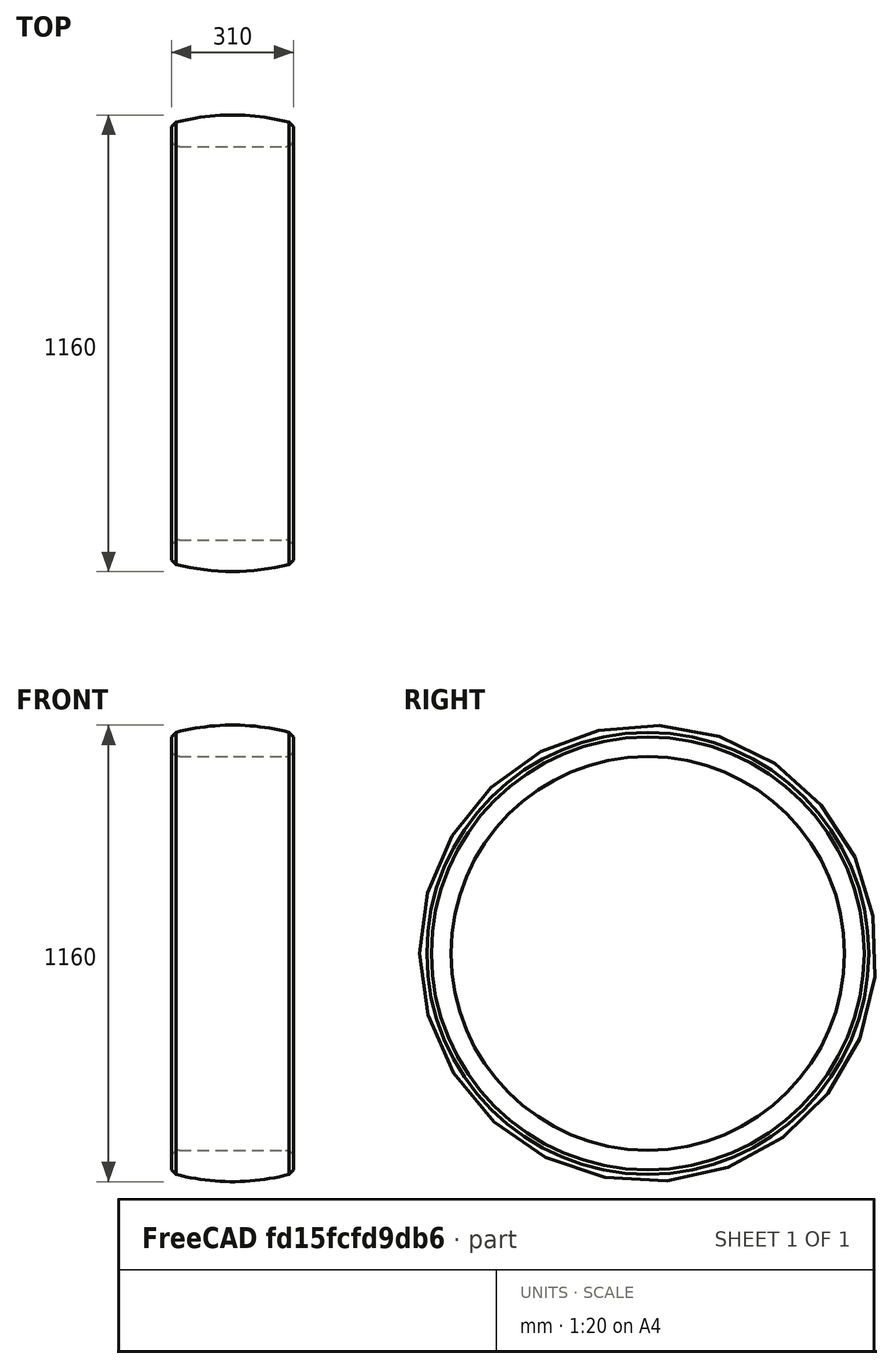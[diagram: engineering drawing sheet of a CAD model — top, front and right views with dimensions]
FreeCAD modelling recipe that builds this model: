
FCSTD DOCUMENT
Label: pr_006 
objects: Sketcher::SketchObject×1, PartDesign::Revolution×1
note: 2 computed .brp shape members not serialized (recipe doc carries the construction recipe); baked Part::Feature solids carry a one-line shape summary decoded from their .brp

FEATURE [Sketcher::SketchObject] Sketch
  sketch-geometry (9):
    g0: ArcOfCircle CenterX=-135 CenterY=-520 CenterZ=0 NormalX=0 NormalY=0 NormalZ=1 Radius=20 StartAngle=1.5708 EndAngle=3.14159
    g1: ArcOfCircle CenterX=135 CenterY=-520 CenterZ=0 NormalX=0 NormalY=0 NormalZ=1 Radius=20 StartAngle=0 EndAngle=1.5708
    g2: LineSegment StartX=-135 StartY=-500 StartZ=0 EndX=135 EndY=-500 EndZ=0
    g3: LineSegment [constr] StartX=-216.428 StartY=-580 StartZ=0 EndX=233.539 EndY=-580 EndZ=0
    g4: LineSegment StartX=-155 StartY=-520 StartZ=0 EndX=-155 EndY=-550 EndZ=0
    g5: LineSegment StartX=155 StartY=-520 StartZ=0 EndX=155 EndY=-550 EndZ=0
    g6: LineSegment StartX=-155 StartY=-550 StartZ=0 EndX=-143.889 EndY=-561.506 EndZ=0
    g7: LineSegment StartX=155 StartY=-550 StartZ=0 EndX=143.889 EndY=-561.506 EndZ=0
    g8: ArcOfCircle CenterX=0 CenterY=-11 CenterZ=0 NormalX=0 NormalY=0 NormalZ=1 Radius=569 StartAngle=4.45673 EndAngle=4.96804
  constraints (25):
    c: Radius(g0) = 20
    c: Radius(g1) = 20
    c: Horizontal(g2)
    c: Tangent(g0,g2)
    c: Tangent(g2,g1)
    c: Horizontal(g3)
    c: DistanceY(g3,g0) = 80
    c: Vertical(g4)
    c: Tangent(g4,g0)
    c: Vertical(g5)
    c: Tangent(g1,g5)
    c: Coincident(g6,g4)
    c: DistanceY(g5,g3) = -30
    c: DistanceY(g4,g3) = -30
    c: Angle(g6,g4) = 2.37365
    c: DistanceX(g0,g1) = 270
    c: DistanceX(g1) = 135
    c: Coincident(g7,g5)
    c: Angle(g5,g7) = 2.37365
    c: Radius(g8) = 569
    c: Tangent(g8,g3)
    c: Coincident(g8,g7)
    c: Coincident(g6,g8)
    c: DistanceY(g1) = -500
    c: DistanceX(g8) = 0
FEATURE [PartDesign::Revolution] Revolution001
  Angle = 360
  Axis = (1,0,0)
  Base = (0,0,0)
  Sketch = -> Sketch
